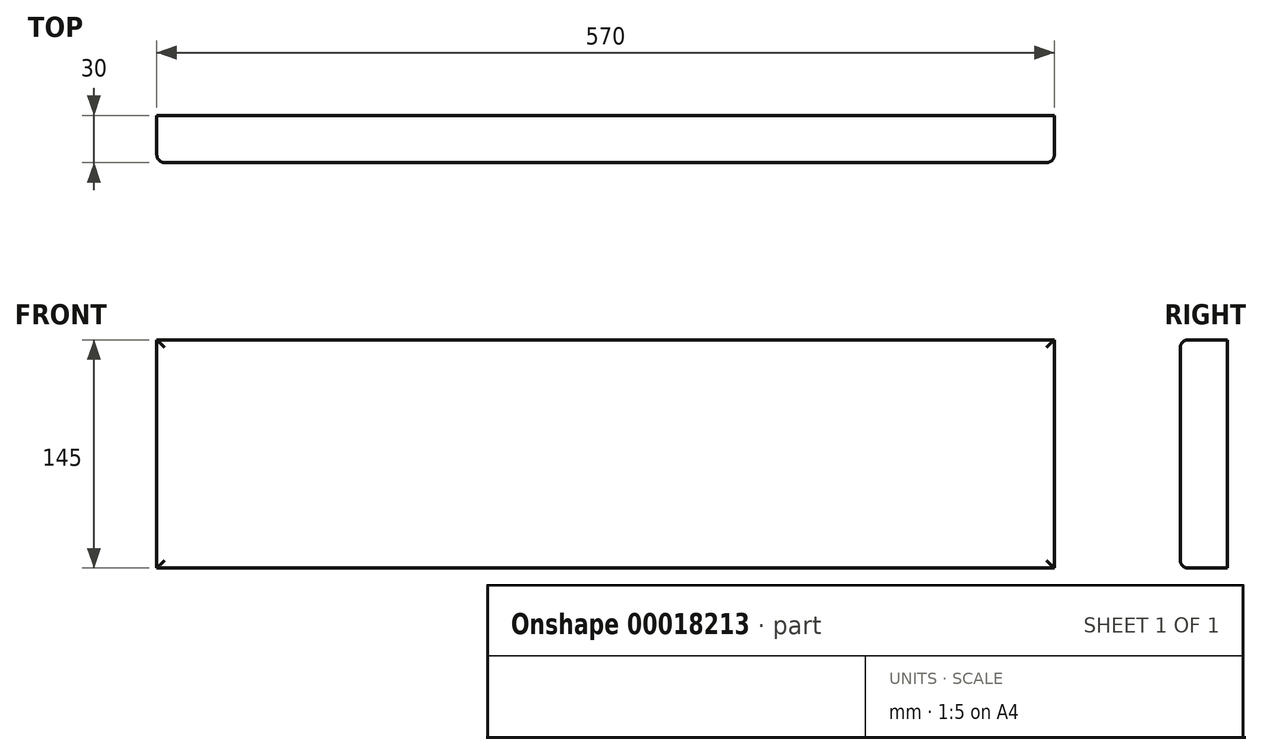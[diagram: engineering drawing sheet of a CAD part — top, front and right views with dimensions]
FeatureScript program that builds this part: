
annotation { "Feature Type Name" : "Feature", "Feature Type Description" : "" }
export const myFeature = defineFeature(function(context is Context, id is Id, definition is map)
    precondition{}
    {
        {
            var Q0;
            Q0=qCreatedBy(makeId("Front.planeOp"),FACE);
            var sketch = newSketch(context, id + "F0", { "sketchPlane" : qUnion([Q0])});
            skLineSegment(sketch, "E0.rect.bottom", {"start": v(285, 72.5) * mm, "end": v(-285, 72.5) * mm});
            skLineSegment(sketch, "E0.rect.top", {"start": v(285, -72.5) * mm, "end": v(-285, -72.5) * mm});
            skLineSegment(sketch, "E0.rect.left", {"start": v(285, 72.5) * mm, "end": v(285, -72.5) * mm});
            skLineSegment(sketch, "E0.rect.right", {"start": v(-285, 72.5) * mm, "end": v(-285, -72.5) * mm});
            skPoint(sketch, "E0.rect.middle", {"position": v(0, 0) * mm});
            skSolve(sketch);
        }
        {
            var Q0;
            Q0 = qSketchRegion(id + "F0", true);
            extrude(context, id + "F1", {"entities" : qUnion([Q0]), "depth" : 30 * mm});
        }
        {
            var Q0;
            Q0=makeQuery(id+"F1.opExtrude","CAP_EDGE",EDGE,{"disambiguationData":[OSD([sQuery(id+"F0.wireOp",EDGE,"E0.rect.right")])],"isStart":false});
            var Q1;
            Q1=makeQuery(id+"F1.opExtrude","CAP_EDGE",EDGE,{"disambiguationData":[OSD([sQuery(id+"F0.wireOp",EDGE,"E0.rect.bottom")])],"isStart":false});
            var Q2;
            Q2=makeQuery(id+"F1.opExtrude","CAP_FACE",FACE,{"disambiguationData":[OSD([sQuery(id+"F0.wireOp",EDGE,"E0.rect.bottom"),sQuery(id+"F0.wireOp",EDGE,"E0.rect.top"),sQuery(id+"F0.wireOp",EDGE,"E0.rect.left"),sQuery(id+"F0.wireOp",EDGE,"E0.rect.right")])],"isStart":false});
            fillet(context, id + "F2", {"entities" : qUnion([Q0, Q1, Q2]), "radius" : 5 * mm, "tangentPropagation" : true, "allowEdgeOverflow" : false});
        }
    });
